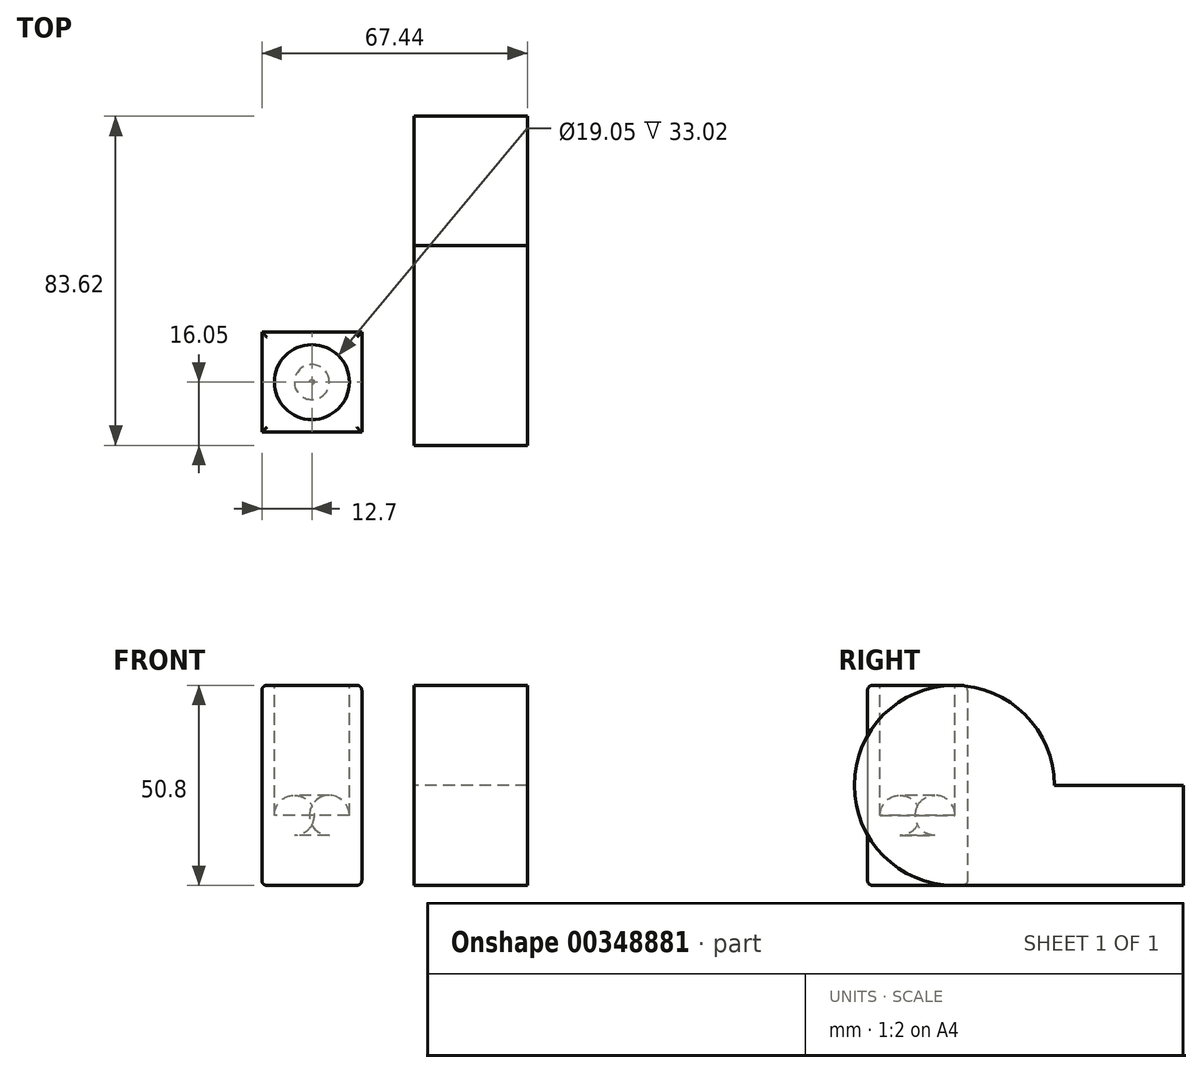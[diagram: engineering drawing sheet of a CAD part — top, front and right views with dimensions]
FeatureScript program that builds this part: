
annotation { "Feature Type Name" : "Feature", "Feature Type Description" : "" }
export const myFeature = defineFeature(function(context is Context, id is Id, definition is map)
    precondition{}
    {
        {
            var Q0;
            Q0=qCreatedBy(makeId("Top.planeOp"),FACE);
            var sketch = newSketch(context, id + "F0", { "sketchPlane" : qUnion([Q0])});
            skLineSegment(sketch, "E0.bottom", {"start": v(12.7, -12.7) * mm, "end": v(-12.7, -12.7) * mm});
            skLineSegment(sketch, "E0.top", {"start": v(12.7, 12.7) * mm, "end": v(-12.7, 12.7) * mm});
            skLineSegment(sketch, "E0.left", {"start": v(12.7, -12.7) * mm, "end": v(12.7, 12.7) * mm});
            skLineSegment(sketch, "E0.right", {"start": v(-12.7, -12.7) * mm, "end": v(-12.7, 12.7) * mm});
            skPoint(sketch, "E0.middle", {"position": v(0, 0) * mm});
            skSolve(sketch);
        }
        {
            var Q0;
            Q0=makeQuery(id+"F0.imprint","IMPRINT",FACE,{"disambiguationData":[TD([[makeQuery(id+"F0.imprint","IMPRINT",EDGE,{"derivedFrom":sQuery(id+"F0.wireOp",EDGE,"E0.bottom")}),-1.0]])]});
            extrude(context, id + "F1", {"entities" : qUnion([Q0]), "depth" : 50.8 * mm});
        }
        {
            var Q0;
            Q0=makeQuery(id+"F1.opExtrude","CAP_FACE",FACE,{"disambiguationData":[OSD([sQuery(id+"F0.wireOp",EDGE,"E0.bottom"),sQuery(id+"F0.wireOp",EDGE,"E0.top"),sQuery(id+"F0.wireOp",EDGE,"E0.left"),sQuery(id+"F0.wireOp",EDGE,"E0.right")])],"isStart":false});
            var sketch = newSketch(context, id + "F2", { "sketchPlane" : qUnion([Q0])});
            skCircle(sketch, "E1", {"center": v(0, 0) * mm, "radius": 9.52 * mm});
            skSolve(sketch);
        }
        {
            var Q0;
            Q0=makeQuery(id+"F2.imprint","IMPRINT",FACE,{"disambiguationData":[TD([[makeQuery(id+"F2.imprint","IMPRINT",EDGE,{"derivedFrom":sQuery(id+"F2.wireOp",EDGE,"E1")}),1.0]])]});
            extrude(context, id + "F3", {"entities" : qUnion([Q0]), "operationType" : NewBodyOperationType.REMOVE, "oppositeDirection" : true, "depth" : 38.1 * mm});
        }
        {
            var Q0;
            Q0=makeQuery(id+"F3.boolean.opBoolean","COPY",EDGE,{"derivedFrom":makeQuery(id+"F3.opExtrude","CAP_EDGE",EDGE,{"disambiguationData":[OSD([sQuery(id+"F2.wireOp",EDGE,"E1")])],"isStart":false})});
            fillet(context, id + "F4", {"entities" : qUnion([Q0]), "radius" : 5.08 * mm, "tangentPropagation" : true, "allowEdgeOverflow" : false});
        }
        {
            var Q0;
            Q0=makeQuery(id+"F3.boolean.opBoolean","COPY",EDGE,{"derivedFrom":makeQuery(id+"F3.opExtrude","CAP_EDGE",EDGE,{"disambiguationData":[OSD([sQuery(id+"F2.wireOp",EDGE,"E1")])],"isStart":true})});
            var Q1;
            Q1=makeQuery(id+"F1.opExtrude","CAP_EDGE",EDGE,{"disambiguationData":[OSD([sQuery(id+"F0.wireOp",EDGE,"E0.top")])],"isStart":false});
            var Q2;
            Q2=makeQuery(id+"F1.opExtrude","CAP_EDGE",EDGE,{"disambiguationData":[OSD([sQuery(id+"F0.wireOp",EDGE,"E0.right")])],"isStart":false});
            var Q3;
            Q3=makeQuery(id+"F1.opExtrude","CAP_EDGE",EDGE,{"disambiguationData":[OSD([sQuery(id+"F0.wireOp",EDGE,"E0.bottom")])],"isStart":false});
            var Q4;
            Q4=makeQuery(id+"F1.opExtrude","CAP_EDGE",EDGE,{"disambiguationData":[OSD([sQuery(id+"F0.wireOp",EDGE,"E0.left")])],"isStart":false});
            fillet(context, id + "F5", {"entities" : qUnion([Q0, Q1, Q2, Q3, Q4]), "radius" : 1.27 * mm, "tangentPropagation" : true, "allowEdgeOverflow" : false});
        }
        {
            var Q0;
            Q0=makeQuery(id+"F1.opExtrude","CAP_FACE",FACE,{"disambiguationData":[OSD([sQuery(id+"F0.wireOp",EDGE,"E0.bottom"),sQuery(id+"F0.wireOp",EDGE,"E0.top"),sQuery(id+"F0.wireOp",EDGE,"E0.left"),sQuery(id+"F0.wireOp",EDGE,"E0.right")])],"isStart":true});
            fillet(context, id + "F6", {"entities" : qUnion([Q0]), "radius" : 1.27 * mm, "tangentPropagation" : true, "allowEdgeOverflow" : false});
        }
        {
            var Q0;
            Q0=qCreatedBy(makeId("Top.planeOp"),FACE);
            var sketch = newSketch(context, id + "F7", { "sketchPlane" : qUnion([Q0])});
            skLineSegment(sketch, "E2.bottom", {"start": v(54.74, 67.57) * mm, "end": v(26, 67.57) * mm});
            skLineSegment(sketch, "E2.top", {"start": v(54.74, 9.35) * mm, "end": v(26, 9.35) * mm});
            skLineSegment(sketch, "E2.left", {"start": v(54.74, 67.57) * mm, "end": v(54.74, 9.35) * mm});
            skLineSegment(sketch, "E2.right", {"start": v(26, 67.57) * mm, "end": v(26, 9.35) * mm});
            skSolve(sketch);
        }
        {
            var Q0;
            Q0=makeQuery(id+"F7.imprint","IMPRINT",FACE,{"disambiguationData":[TD([[makeQuery(id+"F7.imprint","IMPRINT",EDGE,{"derivedFrom":sQuery(id+"F7.wireOp",EDGE,"E2.bottom")}),1.0]])]});
            extrude(context, id + "F8", {"entities" : qUnion([Q0]), "depth" : 25.4 * mm, "offsetDistance" : 25.4 * mm});
        }
        {
            var Q0;
            Q0=makeQuery(id+"F8.opExtrude","SWEPT_FACE",FACE,{"disambiguationData":[OSD([sQuery(id+"F7.wireOp",EDGE,"E2.top")])]});
            var Q1;
            Q1=makeQuery(id+"F8.opExtrude","CAP_EDGE",EDGE,{"disambiguationData":[OSD([sQuery(id+"F7.wireOp",EDGE,"E2.top")])],"isStart":false});
            revolve(context, id + "F9", {"operationType" : NewBodyOperationType.ADD, "surfaceOperationType" : NewSurfaceOperationType.NEW, "entities" : qUnion([Q0]), "axis" : qUnion([Q1]), "revolveType" : RevolveType.FULL});
        }
    });
